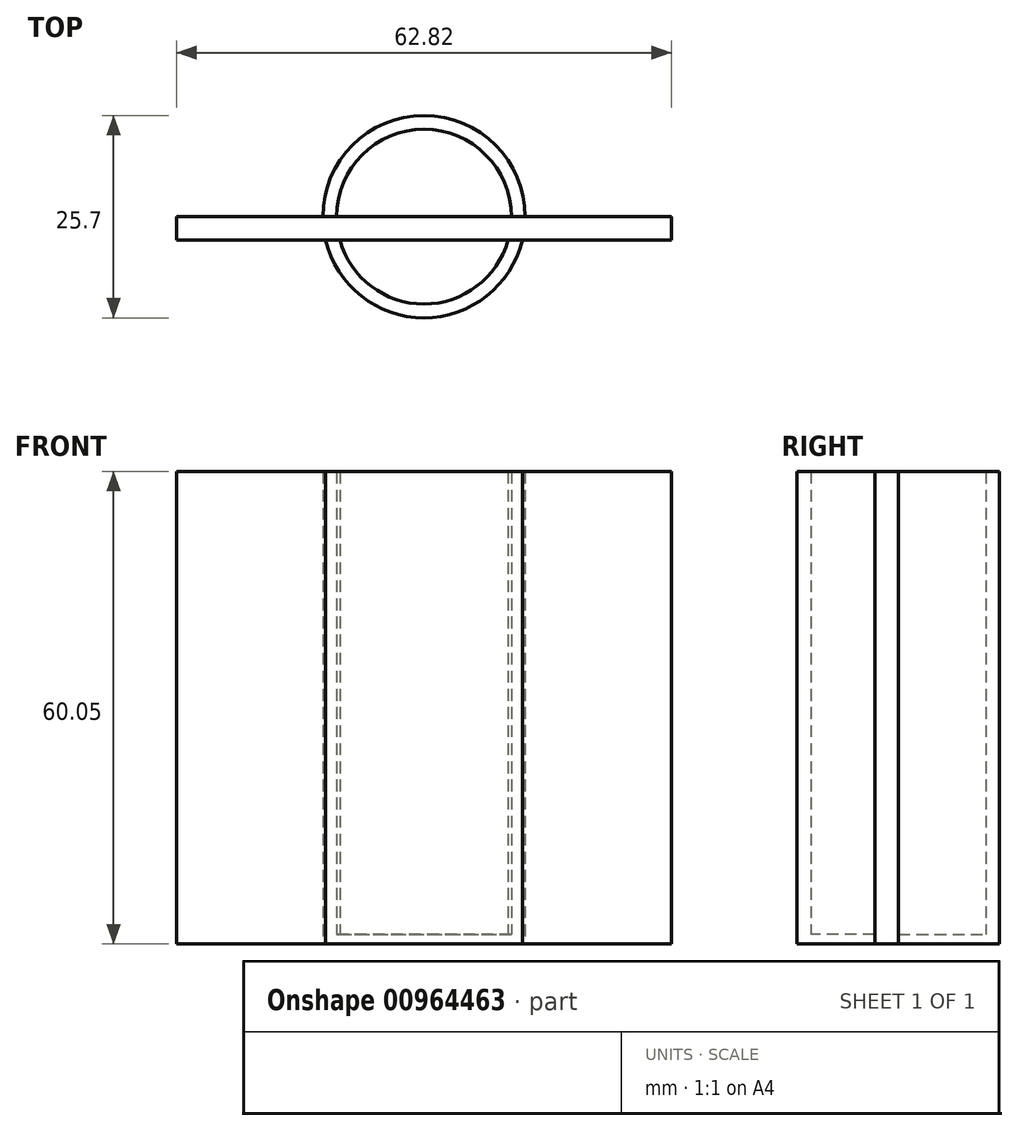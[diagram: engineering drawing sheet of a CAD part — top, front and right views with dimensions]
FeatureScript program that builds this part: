
annotation { "Feature Type Name" : "Feature", "Feature Type Description" : "" }
export const myFeature = defineFeature(function(context is Context, id is Id, definition is map)
    precondition{}
    {
        {
            var Q0;
            Q0=qCreatedBy(makeId("Top.planeOp"),FACE);
            var sketch = newSketch(context, id + "F0", { "sketchPlane" : qUnion([Q0])});
            skCircle(sketch, "E0", {"center": v(0, 0) * mm, "radius": 11.1 * mm});
            skCircle(sketch, "E1", {"center": v(0, 0) * mm, "radius": 12.85 * mm});
            skSolve(sketch);
        }
        {
            var Q0;
            Q0=makeQuery(id+"F0.imprint","IMPRINT",FACE,{"disambiguationData":[TD([[makeQuery(id+"F0.imprint","IMPRINT",EDGE,{"derivedFrom":sQuery(id+"F0.wireOp",EDGE,"E0")}),1.0]])]});
            extrude(context, id + "F1", {"entities" : qUnion([Q0]), "depth" : 1.2 * mm, "offsetDistance" : 25 * mm});
        }
        {
            var Q0;
            Q0=makeQuery(id+"F0.imprint","IMPRINT",FACE,{"disambiguationData":[TD([[makeQuery(id+"F0.imprint","IMPRINT",EDGE,{"derivedFrom":sQuery(id+"F0.wireOp",EDGE,"E0")}),-1.0]])]});
            extrude(context, id + "F2", {"entities" : qUnion([Q0]), "operationType" : NewBodyOperationType.ADD, "depth" : 60 * mm, "offsetDistance" : 25 * mm});
        }
        {
            var Q0;
            Q0=qCreatedBy(makeId("Front.planeOp"),FACE);
            var sketch = newSketch(context, id + "F3", { "sketchPlane" : qUnion([Q0])});
            skLineSegment(sketch, "E2", {"start": v(0, 0) * mm, "end": v(0, 60.05) * mm, "construction": true});
            skLineSegment(sketch, "E3.bottom", {"start": v(-31.4, 0) * mm, "end": v(31.4, 0) * mm});
            skLineSegment(sketch, "E3.top", {"start": v(-31.4, 60.05) * mm, "end": v(31.4, 60.05) * mm});
            skLineSegment(sketch, "E3.left", {"start": v(-31.4, 0) * mm, "end": v(-31.4, 60.05) * mm});
            skLineSegment(sketch, "E3.right", {"start": v(31.4, 0) * mm, "end": v(31.4, 60.05) * mm});
            skPoint(sketch, "E3.middle", {"position": v(0, 30.02) * mm});
            skSolve(sketch);
        }
        {
            var Q0;
            Q0=makeQuery(id+"F3.imprint","IMPRINT",FACE,{"disambiguationData":[TD([[makeQuery(id+"F3.imprint","IMPRINT",EDGE,{"derivedFrom":sQuery(id+"F3.wireOp",EDGE,"E3.bottom")}),1.0]])]});
            extrude(context, id + "F4", {"entities" : qUnion([Q0]), "operationType" : NewBodyOperationType.ADD, "depth" : 3 * mm, "offsetDistance" : 25 * mm});
        }
    });
